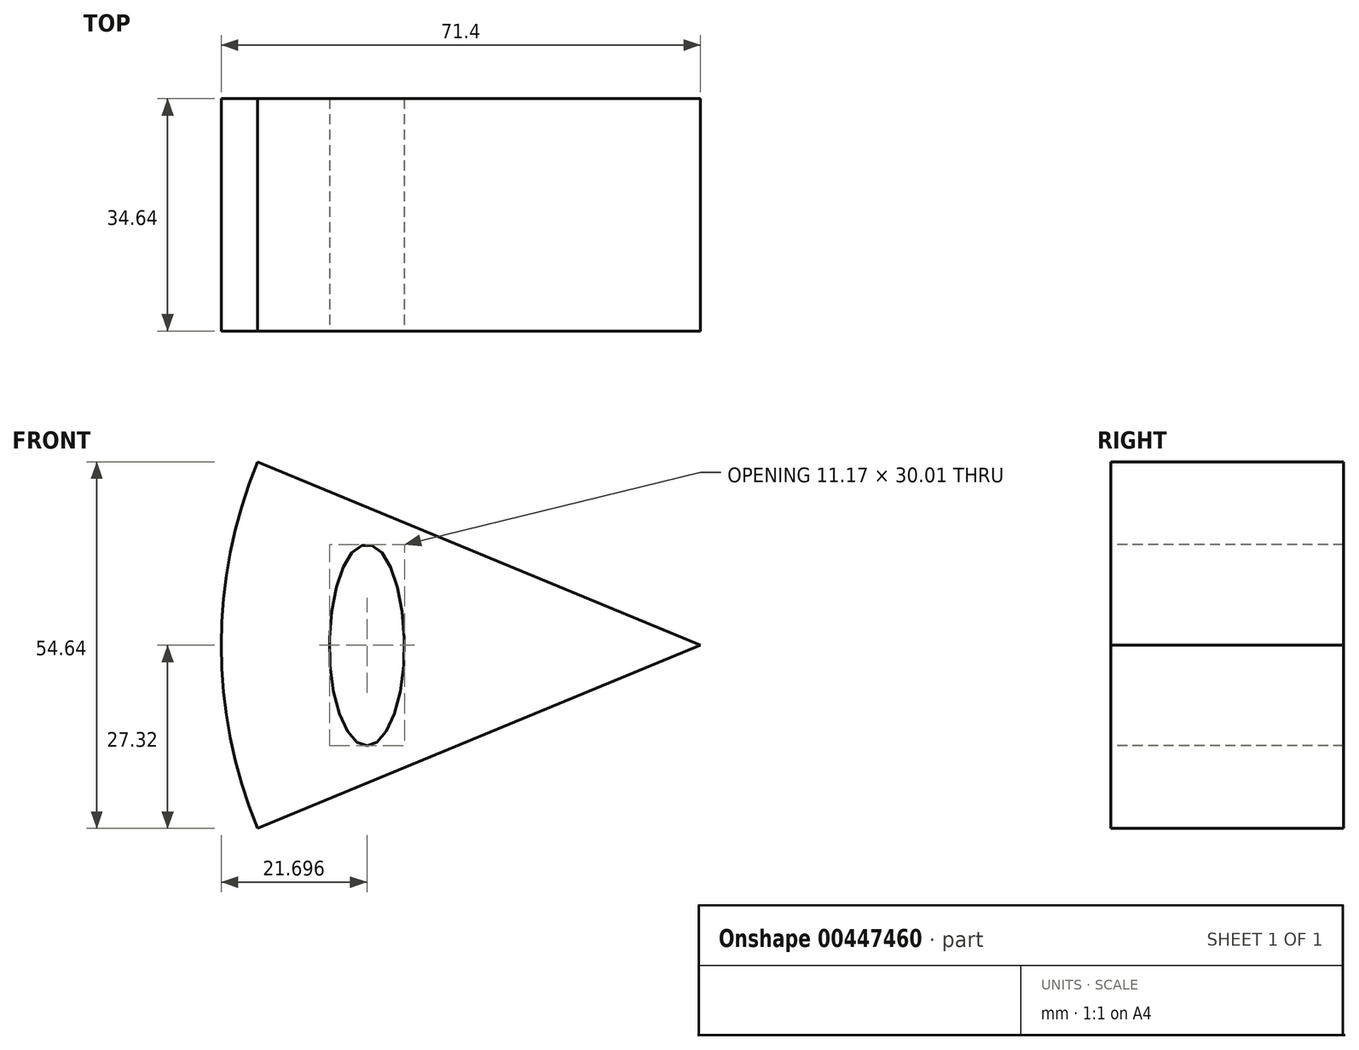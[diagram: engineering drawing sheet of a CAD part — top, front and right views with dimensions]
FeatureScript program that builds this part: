
annotation { "Feature Type Name" : "Feature", "Feature Type Description" : "" }
export const myFeature = defineFeature(function(context is Context, id is Id, definition is map)
    precondition{}
    {
        {
            var Q0;
            Q0=qCreatedBy(makeId("Top.planeOp"),FACE);
            var sketch = newSketch(context, id + "F0", { "sketchPlane" : qUnion([Q0])});
            skLineSegment(sketch, "E0.bottom", {"start": v(-9.74, 42.63) * mm, "end": v(61.66, 42.63) * mm});
            skLineSegment(sketch, "E0.top", {"start": v(-9.74, 7.99) * mm, "end": v(61.66, 7.99) * mm});
            skLineSegment(sketch, "E0.left", {"start": v(-9.74, 42.63) * mm, "end": v(-9.74, 7.99) * mm});
            skLineSegment(sketch, "E0.right", {"start": v(61.66, 42.63) * mm, "end": v(61.66, 7.99) * mm});
            skSolve(sketch);
        }
        {
            var Q0;
            Q0=makeQuery(id+"F0.imprint","IMPRINT",FACE,{"disambiguationData":[TD([[makeQuery(id+"F0.imprint","IMPRINT",EDGE,{"derivedFrom":sQuery(id+"F0.wireOp",EDGE,"E0.bottom")}),-1.0]])]});
            var Q1;
            Q1=sQuery(id+"F0.wireOp",EDGE,"E0.right");
            revolve(context, id + "F1", {"surfaceOperationType" : NewSurfaceOperationType.NEW, "entities" : qUnion([Q0]), "axis" : qUnion([Q1]), "revolveType" : RevolveType.SYMMETRIC, "angle" : 45 * degree});
        }
        {
            var Q0;
            Q0=makeQuery(id+"F1.opRevolve","SWEPT_FACE",FACE,{"disambiguationData":[OSD([sQuery(id+"F0.wireOp",EDGE,"E0.top")])]});
            var sketch = newSketch(context, id + "F2", { "sketchPlane" : qUnion([Q0])});
            skEllipse(sketch, "E1", {"center": v(11.96, 0) * mm, "majorRadius": 15 * mm, "minorRadius": 5.59 * mm, "majorAxis": v(0, -1)});
            skSolve(sketch);
        }
        {
            var Q0;
            Q0=makeQuery(id+"F2.imprint","IMPRINT",FACE,{"disambiguationData":[TD([[makeQuery(id+"F2.imprint","IMPRINT",EDGE,{"derivedFrom":sQuery(id+"F2.wireOp",EDGE,"E1")}),1.0]])]});
            var Q1;
            Q1 = qBodyType(qCreatedBy(id + "F2" ,EDGE), BodyType.WIRE);
            var Q2;
            Q2=sQuery(id+"F2.wireOp",EDGE,"E1");
            var Q3;
            Q3=makeQuery(id+"F1.opRevolve","SWEPT_FACE",FACE,{"disambiguationData":[OSD([sQuery(id+"F0.wireOp",EDGE,"E0.bottom")])]});
            var Q4;
            Q4=makeQuery(id+"F1.opRevolve","SWEPT_FACE",FACE,{"disambiguationData":[OSD([sQuery(id+"F0.wireOp",EDGE,"E0.bottom")])]});
            extrude(context, id + "F3", {"entities" : qUnion([Q0]), "operationType" : NewBodyOperationType.REMOVE, "surfaceEntities" : qUnion([Q1, Q2]), "endBound" : BoundingType.UP_TO_SURFACE, "oppositeDirection" : true, "depth" : 25 * mm, "endBoundEntityFace" : qUnion([Q3]), "offsetDistance" : 25 * mm});
        }
    });
